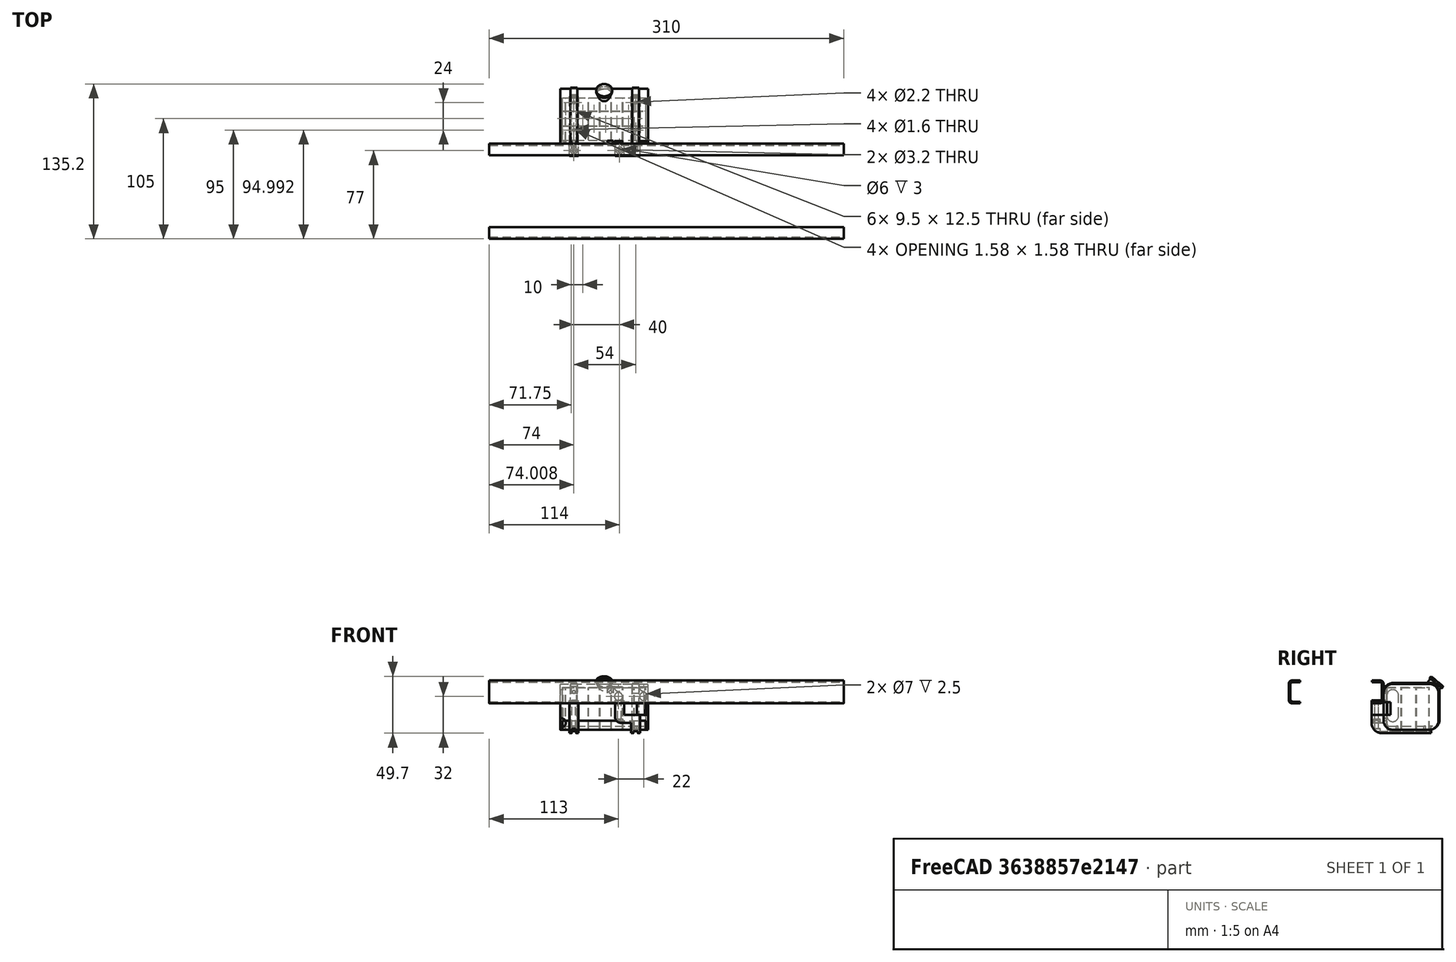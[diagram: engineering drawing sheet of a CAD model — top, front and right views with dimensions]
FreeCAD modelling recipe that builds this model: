
FCSTD DOCUMENT  (FreeCAD 0.15R3918 (Git))
Label: battery-tank
License: CC-BY 3.0
LicenseURL: http://creativecommons.org/licenses/by/3.0/
objects: Part::Box×37, Part::Cylinder×26, Part::Cut×25, Part::MultiFuse×25, Part::Fillet×12, Part::Chamfer×4, Part::Mirroring×1
note: 130 computed .brp shape members not serialized (recipe doc carries the construction recipe); baked Part::Feature solids carry a one-line shape summary decoded from their .brp

FEATURE [Part::Box] Box
  Height = 40
  Length = 77
  Placement = pos=(62,82,-27) rot=(0,0,1;0rad)
  Width = 48
FEATURE [Part::Mirroring] Part__Mirroring  label="Cut (Mirror #1)"
  Base = (0,0,0)
  Normal = (0,1,0)
  Placement = pos=(0,81.5,0) rot=(0,0,1;0rad)
FEATURE [Part::Cut] Cut
  Placement = pos=(0,-1.5,0) rot=(0,0,1;0rad)
FEATURE [Part::MultiFuse] Fusion  label="frame-bars001"
  Placement = pos=(0,0.5,0) rot=(0,0,1;0rad)
  Shapes = -> [Cut,Part__Mirroring]
FEATURE [Part::Fillet] Fillet
  Base = -> Box
  Edges = 4 edges r=8: [Edge9,Edge10,Edge11,Edge12]
  Placement = pos=(0,0,4) rot=(0,0,1;0rad)
FEATURE [Part::Box] Box001
  Height = 40
  Length = 77
  Placement = pos=(62,82,-27) rot=(0,0,1;0rad)
  Width = 48
FEATURE [Part::Fillet] Fillet001
  Base = -> Box001
  Edges = 4 edges r=8: [Edge9,Edge10,Edge11,Edge12]
  Placement = pos=(0,0,4) rot=(0,0,1;0rad)
FEATURE [Part::Box] Box002
  Height = 40
  Length = 73
  Placement = pos=(64,85,-26) rot=(0,0,1;0rad)
  Width = 37
FEATURE [Part::Cut] Cut001
  Base = -> Fillet
  Tool = -> Box002
FEATURE [Part::Box] Box005
  Height = 26
  Length = 8
  Placement = pos=(70,71.5,-26) rot=(0,0,1;0rad)
  Width = 52
FEATURE [Part::Box] Box008
  Height = 40
  Length = 77
  Placement = pos=(62,82,-27) rot=(0,0,1;0rad)
  Width = 48
FEATURE [Part::Fillet] Fillet002
  Base = -> Box008
  Edges = 4 edges r=8: [Edge9,Edge10,Edge11,Edge12]
  Placement = pos=(0,0,4) rot=(0,0,1;0rad)
FEATURE [Part::Cut] Cut002
  Base = -> Box005
  Tool = -> Fillet002
FEATURE [Part::Box] Box009
  Height = 1.5
  Length = 4
  Placement = pos=(72,71.5,-26) rot=(0,0,1;0rad)
  Width = 52
FEATURE [Part::Fillet] Fillet003
  Base = -> Cut002
  Edges = 1 edges r=9: [Edge1]
FEATURE [Part::Cut] Cut003
  Base = -> Fillet003
  Tool = -> Box009
FEATURE [Part::Box] Box010
  Height = 8
  Length = 73
  Placement = pos=(64,82,-23) rot=(0,0,1;0rad)
  Width = 10
FEATURE [Part::Cut] Cut004
  Base = -> Cut001
  Tool = -> Box010
FEATURE [Part::Box] Box011
  Height = 8
  Length = 73
  Placement = pos=(64,82,-23) rot=(0,0,1;0rad)
  Width = 3
FEATURE [Part::Box] Box012
  Height = 3
  Length = 73
  Placement = pos=(64,85,-23) rot=(0,0,1;0rad)
  Width = 37
FEATURE [Part::MultiFuse] Fusion001
  Shapes = -> [Box011,Box012]
FEATURE [Part::Fillet] Fillet004
  Base = -> Fusion001
  Edges = 1 edges r=7.99: [Edge8]
FEATURE [Part::Fillet] Fillet005
  Base = -> Fillet004
  Edges = 1 edges r=2: [Edge20]
FEATURE [Part::Box] Box013
  Height = 41
  Length = 6
  Placement = pos=(71,82,-23) rot=(0,0,1;0rad)
  Width = 49
FEATURE [Part::Fillet] Fillet006
  Base = -> Box013
  Edges = 4 edges r=9: [Edge9,Edge10,Edge11,Edge12]
FEATURE [Part::Box] Box014
  Height = 41
  Length = 6
  Placement = pos=(71,82,-23) rot=(0,0,1;0rad)
  Width = 49
FEATURE [Part::Fillet] Fillet007
  Base = -> Box014
  Edges = 4 edges r=9: [Edge9,Edge10,Edge11,Edge12]
  Placement = pos=(54,0,0) rot=(0,0,1;0rad)
FEATURE [Part::MultiFuse] Fusion002
  Shapes = -> [Fillet006,Fillet007]
FEATURE [Part::Cut] Cut005
  Base = -> Fusion002
  Tool = -> Fillet001
FEATURE [Part::Cylinder] Cylinder
  Angle = 360
  Height = 10
  Placement = pos=(51,75,-3) rot=(0,-1,0;0.523599rad)
  Radius = 6
FEATURE [Part::Cylinder] Cylinder001
  Angle = 360
  Height = 2
  Placement = pos=(51,75,-3) rot=(0,-1,0;0.523599rad)
  Radius = 7
FEATURE [Part::MultiFuse] Fusion004
  Placement = pos=(175.5,143.465,-29.7488) rot=(0.633687,-0.633687,0.443713;2.30637rad)
  Shapes = -> [Cylinder,Cylinder001]
FEATURE [Part::Cylinder] Cylinder004
  Angle = 360
  Height = 4
  Placement = pos=(74,79,-26) rot=(0,0,1;0rad)
  Radius = 3
FEATURE [Part::Cylinder] Cylinder005
  Angle = 360
  Height = 28
  Placement = pos=(74,79,-26) rot=(0,0,1;0rad)
  Radius = 1.6
FEATURE [Part::MultiFuse] Fusion006
  Placement = pos=(0,-3,0) rot=(0,0,1;0rad)
  Shapes = -> [Cylinder004,Cylinder005]
FEATURE [Part::Cut] Cut007
  Base = -> Cut003
  Tool = -> Fusion006
FEATURE [Part::Cylinder] Cylinder006
  Angle = 360
  Height = 28
  Placement = pos=(74,94,-26) rot=(0,0,1;0rad)
  Radius = 1.1
FEATURE [Part::Cylinder] Cylinder007
  Angle = 360
  Height = 28
  Placement = pos=(74,118,-26) rot=(0,0,1;0rad)
  Radius = 1.1
FEATURE [Part::Cylinder] Cylinder008
  Angle = 360
  Height = 28
  Placement = pos=(74,94,-26) rot=(0,0,1;0rad)
  Radius = 0.8
FEATURE [Part::Cylinder] Cylinder009
  Angle = 360
  Height = 28
  Placement = pos=(74,118,-26) rot=(0,0,1;0rad)
  Radius = 0.8
FEATURE [Part::MultiFuse] Fusion007
  Shapes = -> [Cylinder006,Cylinder007]
FEATURE [Part::Cut] Cut008
  Base = -> Cut007
  Tool = -> Fusion007
FEATURE [Part::Box] Box015
  Height = 26
  Length = 8
  Placement = pos=(70,71.5,-26) rot=(0,0,1;0rad)
  Width = 52
FEATURE [Part::Box] Box016
  Height = 40
  Length = 77
  Placement = pos=(62,82,-27) rot=(0,0,1;0rad)
  Width = 48
FEATURE [Part::Fillet] Fillet009
  Base = -> Box016
  Edges = 4 edges r=8: [Edge9,Edge10,Edge11,Edge12]
  Placement = pos=(0,0,4) rot=(0,0,1;0rad)
FEATURE [Part::Cut] Cut012
  Base = -> Box015
  Tool = -> Fillet009
FEATURE [Part::Fillet] Fillet008
  Base = -> Cut012
  Edges = 1 edges r=9: [Edge1]
FEATURE [Part::Box] Box017
  Height = 1.5
  Length = 4
  Placement = pos=(72,71.5,-26) rot=(0,0,1;0rad)
  Width = 52
FEATURE [Part::Cut] Cut011
  Base = -> Fillet008
  Placement = pos=(54,0,0) rot=(0,0,1;0rad)
  Tool = -> Box017
FEATURE [Part::Cylinder] Cylinder010
  Angle = 360
  Height = 4
  Placement = pos=(74,79,-26) rot=(0,0,1;0rad)
  Radius = 3
FEATURE [Part::Cylinder] Cylinder011
  Angle = 360
  Height = 28
  Placement = pos=(74,79,-26) rot=(0,0,1;0rad)
  Radius = 1.6
FEATURE [Part::MultiFuse] Fusion008
  Placement = pos=(40,-3,8) rot=(0,0,1;0rad)
  Shapes = -> [Cylinder010,Cylinder011]
FEATURE [Part::Cylinder] Cylinder012
  Angle = 360
  Height = 28
  Placement = pos=(74,94,-26) rot=(0,0,1;0rad)
  Radius = 1.1
FEATURE [Part::Cylinder] Cylinder013
  Angle = 360
  Height = 28
  Placement = pos=(74,118,-26) rot=(0,0,1;0rad)
  Radius = 1.1
FEATURE [Part::MultiFuse] Fusion009
  Placement = pos=(54,0,0) rot=(0,0,1;0rad)
  Shapes = -> [Cylinder012,Cylinder013]
FEATURE [Part::MultiFuse] Fusion010
  Shapes = -> [Cylinder008,Cylinder009]
FEATURE [Part::Cylinder] Cylinder014
  Angle = 360
  Height = 28
  Placement = pos=(74,118,-26) rot=(0,0,1;0rad)
  Radius = 0.8
FEATURE [Part::Cylinder] Cylinder015
  Angle = 360
  Height = 28
  Placement = pos=(74,94,-26) rot=(0,0,1;0rad)
  Radius = 0.8
FEATURE [Part::MultiFuse] Fusion011
  Placement = pos=(54,0,0) rot=(0,0,1;0rad)
  Shapes = -> [Cylinder015,Cylinder014]
FEATURE [Part::MultiFuse] Fusion012
  Shapes = -> [Fusion010,Fusion011]
FEATURE [Part::Cut] Cut013
  Base = -> Fillet005
  Tool = -> Fusion012
FEATURE [Part::Box] Box018
  Height = 10
  Length = 5
  Placement = pos=(71.5,82,5) rot=(0,0,1;0rad)
  Width = 3
FEATURE [Part::Box] Box020
  Height = 3
  Length = 6
  Placement = pos=(70,113,-23) rot=(0,0,1;0rad)
  Width = 3
FEATURE [Part::Chamfer] Chamfer
  Base = -> Box020
  Edges = 1 edges r=2.99: [Edge11]
  Placement = pos=(1,9,0.5) rot=(0,0,1;0rad)
FEATURE [Part::Box] Box021
  Height = 2.5
  Length = 5
  Placement = pos=(70.5,113,-22.5) rot=(0,0,1;0rad)
  Width = 2.5
FEATURE [Part::Chamfer] Chamfer001
  Base = -> Box021
  Edges = 1 edges r=2.49: [Edge11]
  Placement = pos=(1,9,0) rot=(0,0,1;0rad)
FEATURE [Part::Box] Box022
  Height = 3
  Length = 6
  Placement = pos=(70,113,-23) rot=(0,0,1;0rad)
  Width = 3
FEATURE [Part::Chamfer] Chamfer002
  Base = -> Box022
  Edges = 1 edges r=2.99: [Edge11]
  Placement = pos=(55,9,0.5) rot=(0,0,1;0rad)
FEATURE [Part::Box] Box023
  Height = 2.5
  Length = 5
  Placement = pos=(70.5,113,-22.5) rot=(0,0,1;0rad)
  Width = 2.5
FEATURE [Part::Chamfer] Chamfer003
  Base = -> Box023
  Edges = 1 edges r=2.49: [Edge11]
  Placement = pos=(55,9,0) rot=(0,0,1;0rad)
FEATURE [Part::MultiFuse] Fusion016
  Shapes = -> [Chamfer001,Chamfer003]
FEATURE [Part::MultiFuse] Fusion017
  Shapes = -> [Cut013,Fusion016]
FEATURE [Part::Box] Box024
  Height = 28
  Length = 10
  Placement = pos=(54,85,-16) rot=(0,0,1;0rad)
  Width = 10
FEATURE [Part::Fillet] Fillet010
  Base = -> Box024
  Edges = 4 edges r=4.99: [Edge9,Edge10,Edge11,Edge12]
FEATURE [Part::Box] Box025
  Height = 5
  Length = 20
  Placement = pos=(90,112,9) rot=(0,0,1;0rad)
  Width = 10
FEATURE [Part::Box] Box026 .. Box032  x7 (patterned run collapsed; names and placements below)
  Height = 36.8
  Length = 0.5
  Width = 36.5
  placements: 7 in arithmetic series — first pos=(126.5,85.25,-23) rot=(0,0,1;0rad), step (-10,0,0), last pos=(66.5,85.25,-23) rot=(0,0,1;0rad)
FEATURE [Part::Box] Box033
  Height = 36.8
  Length = 71.5
  Placement = pos=(64.5,97.25,-23) rot=(0,0,1;0rad)
  Width = 0.5
FEATURE [Part::Box] Box034
  Height = 36.8
  Length = 71.5
  Placement = pos=(64.5,110.25,-23) rot=(0,0,1;0rad)
  Width = 0.5
FEATURE [Part::MultiFuse] Fusion019  label="support"
  Shapes = -> [Box026,Box029,Box030,Box034,Box032,Box028,Box027,Box031,Box033]
FEATURE [Part::Cylinder] Cylinder018
  Angle = 360
  Height = 10
  Placement = pos=(-8,25.5,0) rot=(0,0,1;0rad)
  Radius = 3.5
FEATURE [Part::Cylinder] Cylinder019
  Angle = 360
  Height = 10
  Placement = pos=(-8,33.5,0) rot=(0,0,1;0rad)
  Radius = 3.5
FEATURE [Part::MultiFuse] Fusion020
  Placement = pos=(312,84.5,-19.5) rot=(1,0,0;1.5708rad)
  Shapes = -> [Cylinder019,Cylinder018]
FEATURE [Part::Cylinder] Cylinder020
  Angle = 360
  Height = 10
  Placement = pos=(-8,33.5,0) rot=(0,0,1;0rad)
  Radius = 3.5
FEATURE [Part::Cylinder] Cylinder021
  Angle = 360
  Height = 10
  Placement = pos=(-8,25.5,0) rot=(0,0,1;0rad)
  Radius = 3.5
FEATURE [Part::MultiFuse] Fusion022
  Placement = pos=(334,84.5,-19.5) rot=(1,0,0;1.5708rad)
  Shapes = -> [Cylinder020,Cylinder021]
FEATURE [Part::MultiFuse] Fusion023
  Placement = pos=(-191,0,0) rot=(0,0,1;0rad)
  Shapes = -> [Fusion022,Fusion020]
FEATURE [Part::Box] Box035
  Height = 10
  Length = 5
  Placement = pos=(103.5,82,5) rot=(0,0,1;0rad)
  Width = 3
FEATURE [Part::MultiFuse] Fusion028
  Shapes = -> [Chamfer,Chamfer002]
FEATURE [Part::Cut] Cut018
  Base = -> Cut004
  Tool = -> Fusion028
FEATURE [Part::Cut] Cut019
  Base = -> Cut018
  Tool = -> Fillet010
FEATURE [Part::MultiFuse] Fusion029
  Shapes = -> [Fusion004,Cut019]
FEATURE [Part::Cut] Cut020
  Base = -> Fusion029
  Tool = -> Box025
FEATURE [Part::MultiFuse] Fusion030
  Shapes = -> [Cut020,Box018,Box035]
FEATURE [Part::Cylinder] Cylinder023
  Angle = 360
  Height = 15
  Placement = pos=(74,97,10) rot=(1,0,0;1.5708rad)
  Radius = 1.25
FEATURE [Part::Cylinder] Cylinder024
  Angle = 360
  Height = 15
  Placement = pos=(106,97,10) rot=(1,0,0;1.5708rad)
  Radius = 1.25
FEATURE [Part::MultiFuse] Fusion031
  Placement = pos=(0,-8,0) rot=(0,0,1;0rad)
  Shapes = -> [Cylinder024,Cylinder023]
FEATURE [Part::Cut] Cut021
  Base = -> Fusion030
  Tool = -> Fusion023
FEATURE [Part::Cut] Cut022
  Base = -> Cut021
  Tool = -> Fusion031
FEATURE [Part::Box] Box036  label="Cube"
  Height = 11
  Length = 14
  Placement = pos=(129,78,-10) rot=(0,0,1;0rad)
  Width = 10
FEATURE [Part::Cut] Cut023
  Base = -> Cut022
  Tool = -> Box036
FEATURE [Part::Cylinder] Cylinder025
  Angle = 360
  Height = 15
  Placement = pos=(74,97,10) rot=(1,0,0;1.5708rad)
  Radius = 1.25
FEATURE [Part::Cylinder] Cylinder026
  Angle = 360
  Height = 15
  Placement = pos=(106,97,10) rot=(1,0,0;1.5708rad)
  Radius = 1.25
FEATURE [Part::MultiFuse] Fusion032
  Placement = pos=(0,-8,0) rot=(0,0,1;0rad)
  Shapes = -> [Cylinder026,Cylinder025]
FEATURE [Part::Cut] Cut024
  Base = -> Cut005
  Tool = -> Fusion032
FEATURE [Part::Cylinder] Cylinder027
  Angle = 360
  Height = 2.5
  Placement = pos=(63,84.5,-17) rot=(1,0,0;1.5708rad)
  Radius = 4
FEATURE [Part::Cut] Cut025
  Base = -> Cut023
  Tool = -> Cylinder027
FEATURE [Part::Cylinder] Cylinder028
  Angle = 360
  Height = 2.5
  Placement = pos=(63,84.5,-17) rot=(1,0,0;1.5708rad)
  Radius = 4
FEATURE [Part::Cut] Cut026
  Base = -> Fusion017
  Tool = -> Cylinder028
FEATURE [Part::Box] Box037  label="Cube001"
  Height = 10
  Length = 8
  Placement = pos=(124,71.5,-10) rot=(0,0,1;0rad)
  Width = 10.5
FEATURE [Part::Box] Box038  label="Cube002"
  Height = 10
  Length = 8
  Placement = pos=(110,71.5,-10) rot=(0,0,1;0rad)
  Width = 10.5
FEATURE [Part::Cut] Cut027
  Base = -> Cut011
  Tool = -> Box037
FEATURE [Part::Box] Box039  label="Cube003"
  Height = 7
  Length = 15
  Placement = pos=(110,71.5,-17) rot=(0,0,1;0rad)
  Width = 10.5
FEATURE [Part::MultiFuse] Fusion033
  Shapes = -> [Box038,Cut027,Box039]
FEATURE [Part::Fillet] Fillet011
  Base = -> Fusion033
  Edges = 1 edges r=5: [Edge9]
FEATURE [Part::Cut] Cut028
  Base = -> Fillet011
  Tool = -> Fusion008
FEATURE [Part::Cut] Cut029
  Base = -> Cut028
  Tool = -> Fusion009
FEATURE [Part::Box] Box040
  Height = 2.5
  Length = 8
  Placement = pos=(70,71.5,-26) rot=(0,0,1;0rad)
  Width = 10.5
FEATURE [Part::Cylinder] Cylinder030
  Angle = 360
  Height = 28
  Placement = pos=(74,76,-28) rot=(0,0,1;0rad)
  Radius = 1.6
FEATURE [Part::Cut] Cut030
  Base = -> Box040
  Placement = pos=(0,0,26) rot=(0,0,1;0rad)
  Tool = -> Cylinder030
FEATURE [Part::Box] Box041
  Height = 2.5
  Length = 8
  Placement = pos=(70,71.5,-26) rot=(0,0,1;0rad)
  Width = 10.5
FEATURE [Part::Cylinder] Cylinder031
  Angle = 360
  Height = 28
  Placement = pos=(74,76,-28) rot=(0,0,1;0rad)
  Radius = 1.6
FEATURE [Part::Cut] Cut031
  Base = -> Box041
  Placement = pos=(40,0,26) rot=(0,0,1;0rad)
  Tool = -> Cylinder031
FEATURE [Part::MultiFuse] Fusion034
  Shapes = -> [Cut008,Cut030]
FEATURE [Part::MultiFuse] Fusion035
  Shapes = -> [Cut029,Cut031]
